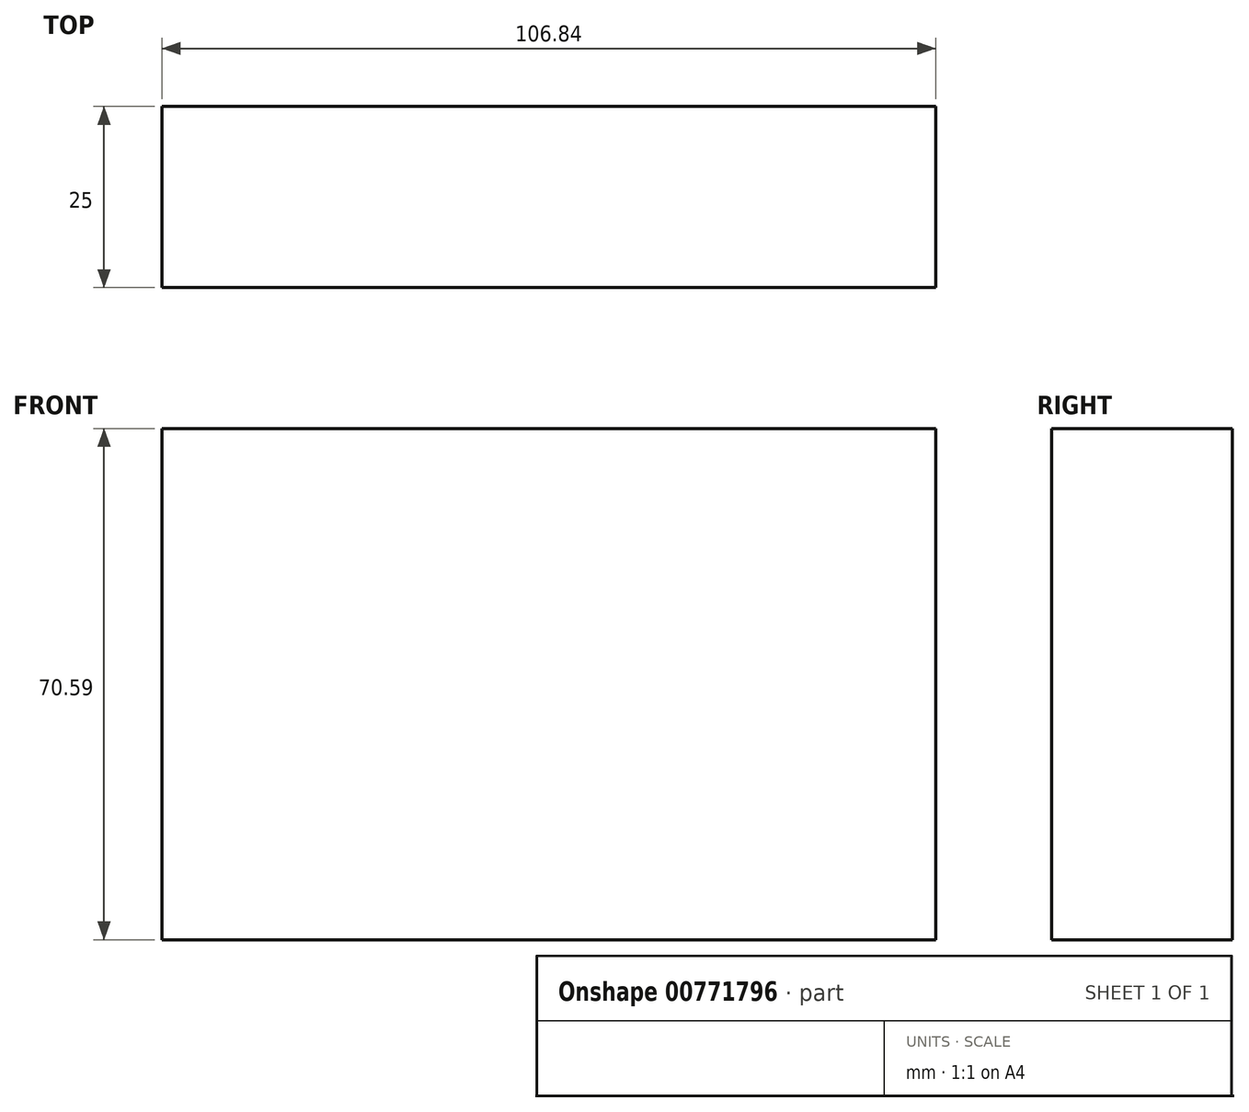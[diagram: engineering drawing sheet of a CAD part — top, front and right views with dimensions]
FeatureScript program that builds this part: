
annotation { "Feature Type Name" : "Feature", "Feature Type Description" : "" }
export const myFeature = defineFeature(function(context is Context, id is Id, definition is map)
    precondition{}
    {
        {
            var Q0;
            Q0=qCreatedBy(makeId("Front.planeOp"),FACE);
            var sketch = newSketch(context, id + "F0", { "sketchPlane" : qUnion([Q0])});
            skLineSegment(sketch, "E0.bottom", {"start": v(-47.06, 37.74) * mm, "end": v(59.78, 37.74) * mm});
            skLineSegment(sketch, "E0.top", {"start": v(-47.06, -32.85) * mm, "end": v(59.78, -32.85) * mm});
            skLineSegment(sketch, "E0.left", {"start": v(-47.06, 37.74) * mm, "end": v(-47.06, -32.85) * mm});
            skLineSegment(sketch, "E0.right", {"start": v(59.78, 37.74) * mm, "end": v(59.78, -32.85) * mm});
            skSolve(sketch);
        }
        {
            var Q0;
            Q0 = qSketchRegion(id + "F0", true);
            extrude(context, id + "F1", {"entities" : qUnion([Q0]), "depth" : 25 * mm, "offsetDistance" : 25 * mm});
        }
    });
